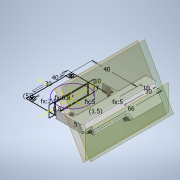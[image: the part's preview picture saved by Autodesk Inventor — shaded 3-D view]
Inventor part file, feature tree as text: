
AUTODESK INVENTOR PART (.ipt)
format: ipt  version: 2020.2 (Build 242310000, 310)  size: 799,744 bytes
history: native  units: mm
features: extrude x16, draft x9, sketch x7, plane x7, fillet x4, projected_geometry x3, thicken_offset x2, shell x1
ambient origin geometry x8: Origin, YZ Plane, XZ Plane, XY Plane, X Axis, Y Axis, Z Axis, Center Point
bodies: Solid1 (feature_tree), Solid3 (feature_tree)
feature tree (49):
  sketch  "Sketch2"  dims[d0=40.0mm d1=40.0mm]
  sketch  "Sketch15"  dims[d6=10.0mm d7=5.0mm]
  plane  "Work Plane1"
  sketch  "Sketch3"  dims[d2=2.5mm d3=30.0mm]
  sketch  "Sketch5"  dims[d4=5.0mm d5=3.0mm]
  plane  "Work Plane2"
  extrude  "Extrusion1"  Depth=40.0mm
  extrude  "Extrusion2"  Depth=30.0mm
  extrude  "Extrusion12"  Depth=5.0mm
  extrude  "Extrusion3"  Depth=5.0mm
  extrude  "Extrusion4"  TaperAngle=0.0deg  [1 undecoded]
  extrude  "Extrusion10"  Depth=1.4mm TaperAngle=0.0deg
  extrude  "Extrusion5"  TaperAngle=0.0deg  [1 undecoded]
  plane  "Work Plane4"
  plane  "Work Plane7"
  extrude  "Extrusion28"  Depth=0.8mm
  extrude  "Extrusion29"  Depth=0.8mm
  draft  "FaceDraft20"
  draft  "FaceDraft21"
  draft  "FaceDraft22"
  draft  "FaceDraft23"
  draft  "FaceDraft25"
  draft  "FaceDraft26"
  draft  "FaceDraft28"
  extrude  "Extrusion31"  Depth=20.0mm
  draft  "FaceDraft29"
  shell  "Shell4"  Thickness=0.0mm
  extrude  "Extrusion33"  Depth=20.0mm
  extrude  "Extrusion34"  Depth=5.0mm
  extrude  "Extrusion39"  TaperAngle=0.0deg  [1 undecoded]
  extrude  "Extrusion35"  Depth=1.5mm
  draft  "FaceDraft30"
  extrude  "Extrusion37"  Depth=66.0mm
  extrude  "Extrusion36"  [1 undecoded]
  fillet  "Fillet26"  Radius=30.0mm
  fillet  "Fillet27"  Radius=0.5mm
  fillet  "Fillet22"  Radius=5.0mm
  fillet  "Fillet25"  Radius=10.0mm
  thicken_offset  "Thicken14"
  thicken_offset  "Thicken15"
  plane  "Work Plane16"
  plane  "Work Plane17"
  plane  "Work Plane18"
  sketch  "Sketch18"  dims[d8=1.4mm d9=0.0mm]
  projected_geometry  "Projected Loop4"
  sketch  "Sketch19"  dims[d10=0.0mm d11=1.4mm d12=0.0mm]
  projected_geometry  "Projected Loop5"
  sketch  "Sketch21"  dims[d13=5.0mm d14=0.0mm d15=0.8mm d16=0.8mm d17=20.0mm d18=0.0mm d19=20.0mm d25=5.0mm d26=0.0mm d28=1.5mm d36=66.0mm d44=-5.0mm d69=30.0mm d71=0.5mm d72=0.0mm d76=5.0mm d77=0.0mm d112=10.0mm d121=12.0mm d122=0.0mm d126=-12.0mm d168=5.0mm d188=30.0deg d198=15.0mm d210=5.0mm d211=5.0mm d212=0.0mm d213=11.0mm d214=0.0mm d217=30.0deg d218=30.0deg d225=0.8mm d226=30.0deg d227=30.0deg d228=5.0mm d229=10.0mm d230=0.0mm d235=0.872665mm d236=0.872665mm d238=0.872665mm d239=30.0deg d241=0.0mm d242=0.0mm d243=10.0mm d244=0.0mm d245=30.936mm d246=0.0mm d247=10.0mm d248=0.0mm d249=30.0deg d250=2.0mm d252=10.0mm d253=0.0mm d254=8.0mm d255=1.0mm d256=0.0mm d260=0.0mm d261=0.0mm d265=1.0mm d266=0.0mm d267=8.0mm d268=0.0mm d284=0.4mm d285=2.0mm d286=2.0mm d287=1.0mm d288=1.0mm d289=0.1mm d290=0.1mm d291=0.1mm d292=0.1mm d293=1.0mm d294=90.0deg d295=90.0deg d296=90.0deg d123=0.5mm d124=0.872665mm d125=0.5mm d150=0.5mm d151=0.872665mm d152=0.5mm d153=0.872665mm d189=0.872665mm d190=0.5mm d191=0.872665mm d269=0.5mm d270=0.872665mm d271=0.5mm d272=0.872665mm]
  projected_geometry  "Projected Loop7"
note: 4 required parameter values undecoded (feature->parameter linkage not recoverable at this tier; creation-order binding heuristic only, values carry confidence <= 0.55)
